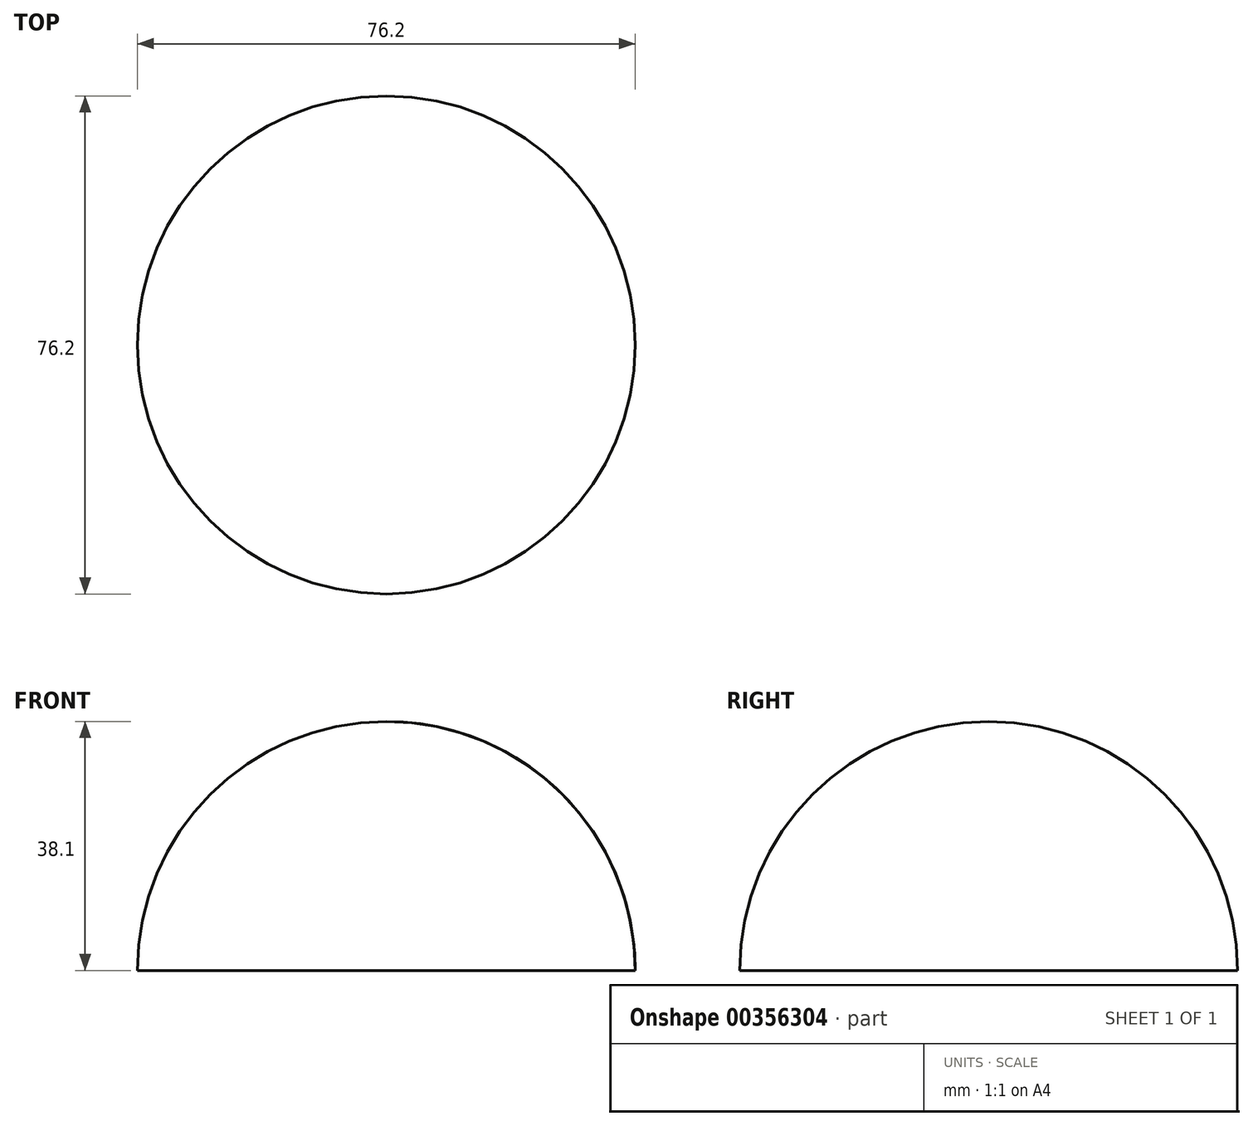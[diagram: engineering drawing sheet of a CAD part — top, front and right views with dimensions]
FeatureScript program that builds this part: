
annotation { "Feature Type Name" : "Feature", "Feature Type Description" : "" }
export const myFeature = defineFeature(function(context is Context, id is Id, definition is map)
    precondition{}
    {
        {
            var Q0;
            Q0=qCreatedBy(makeId("Front.planeOp"),FACE);
            var sketch = newSketch(context, id + "F0", { "sketchPlane" : qUnion([Q0])});
            skArc(sketch, "E0", {"start": v(0, 38.1) * mm, "mid": v(-26.94, 26.94) * mm, "end": v(-38.1, 0) * mm});
            skLineSegment(sketch, "E1", {"start": v(0, 38.1) * mm, "end": v(0, 0) * mm});
            skLineSegment(sketch, "E2", {"start": v(-38.1, 0) * mm, "end": v(0, 0) * mm});
            skSolve(sketch);
        }
        {
            var Q0;
            Q0=qSketchRegion(id+"F0",true);
            var Q1;
            Q1=sQuery(id+"F0.wireOp",EDGE,"E1");
            revolve(context, id + "F1", {"entities" : qUnion([Q0]), "axis" : qUnion([Q1]), "revolveType" : RevolveType.FULL});
        }
    });
